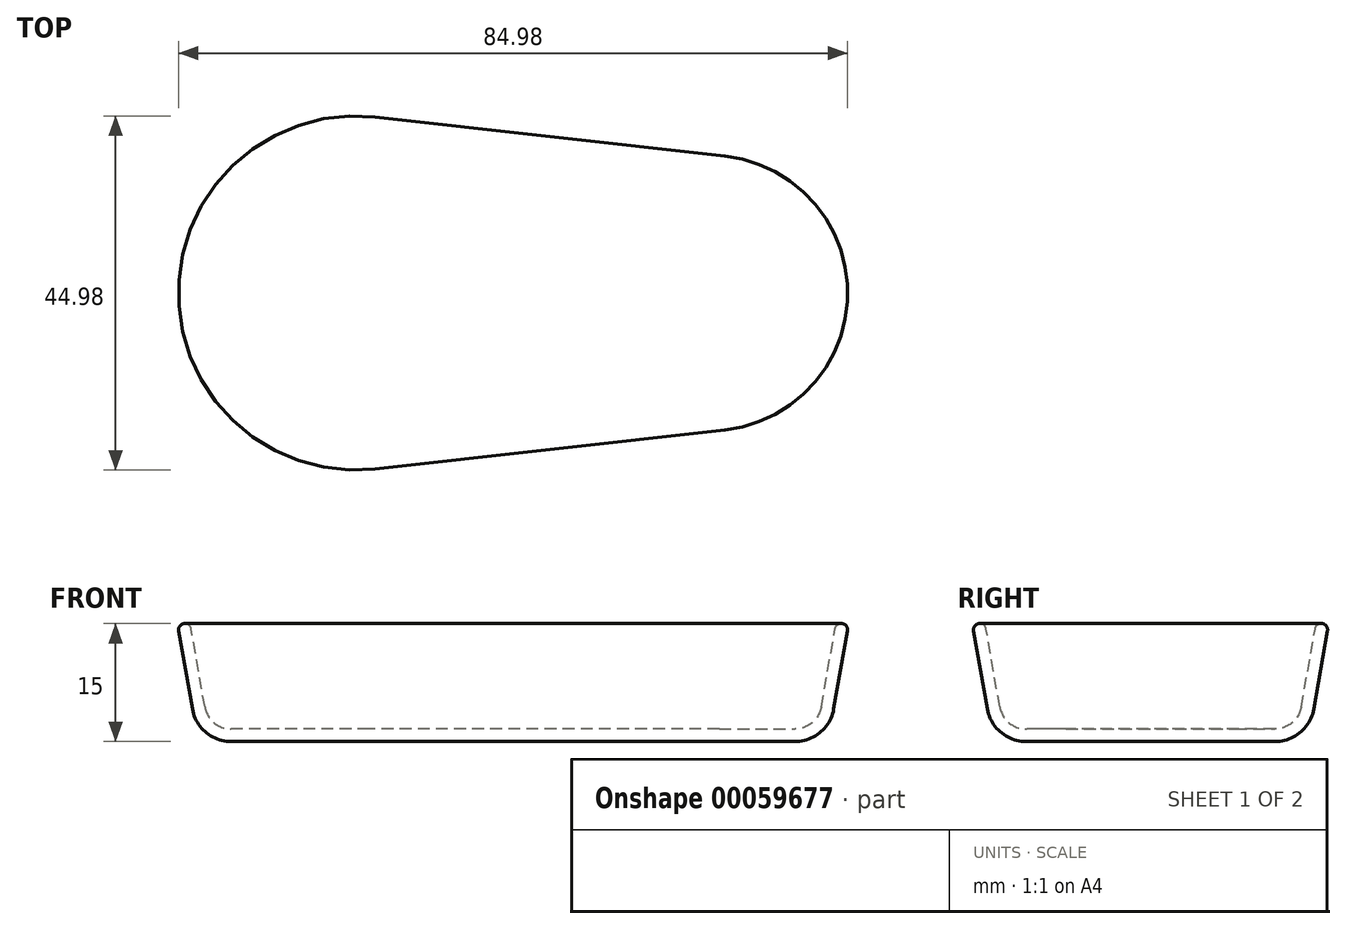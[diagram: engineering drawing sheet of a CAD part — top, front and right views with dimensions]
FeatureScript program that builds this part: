
annotation { "Feature Type Name" : "Feature", "Feature Type Description" : "" }
export const myFeature = defineFeature(function(context is Context, id is Id, definition is map)
    precondition{}
    {
        {
            var Q0;
            Q0=qCreatedBy(makeId("Top.planeOp"),FACE);
            var sketch = newSketch(context, id + "F0", { "sketchPlane" : qUnion([Q0])});
            skLineSegment(sketch, "E0.bottom", {"start": v(-20, 20) * mm, "end": v(60, 20) * mm});
            skLineSegment(sketch, "E0.top", {"start": v(-20, -20) * mm, "end": v(60, -20) * mm});
            skLineSegment(sketch, "E0.left", {"start": v(-20, 20) * mm, "end": v(-20, -20) * mm});
            skLineSegment(sketch, "E0.right", {"start": v(60, 20) * mm, "end": v(60, -20) * mm});
            skArc(sketch, "E1", {"start": v(2.22, 19.88) * mm, "mid": v(-20, 0) * mm, "end": v(2.22, -19.88) * mm});
            skArc(sketch, "E2", {"start": v(46.67, -14.9) * mm, "mid": v(60, 0) * mm, "end": v(46.67, 14.9) * mm});
            skLineSegment(sketch, "E3", {"start": v(2.22, 19.88) * mm, "end": v(46.67, 14.9) * mm});
            skLineSegment(sketch, "E4", {"start": v(2.22, -19.88) * mm, "end": v(46.67, -14.9) * mm});
            skSolve(sketch);
        }
        {
            var Q0;
            {var subQ5=sQuery(id+"F0.wireOp",EDGE,"E3");Q0=makeQuery(id+"F0.imprint","IMPRINT",FACE,{"disambiguationData":[TD([[makeQuery(id+"F0.imprint","IMPRINT",EDGE,{"derivedFrom":subQ5}),-1.0]])]});}
            extrude(context, id + "F1", {"entities" : qUnion([Q0]), "depth" : 15 * mm, "hasDraft" : true, "draftAngle" : 10 * degree});
        }
        {
            var Q0;
            Q0=makeQuery(id+"F1.opExtrude","CAP_EDGE",EDGE,{"disambiguationData":[OSD([sQuery(id+"F0.wireOp",EDGE,"E1")])],"isStart":true});
            fillet(context, id + "F2", {"entities" : qUnion([Q0]), "radius" : 5 * mm, "tangentPropagation" : true, "allowEdgeOverflow" : false});
        }
        {
            var Q0;
            Q0=makeQuery(id+"F1.opExtrude","CAP_FACE",FACE,{"disambiguationData":[OSD([sQuery(id+"F0.wireOp",EDGE,"E0.bottom"),sQuery(id+"F0.wireOp",EDGE,"E0.top"),sQuery(id+"F0.wireOp",EDGE,"E0.left"),sQuery(id+"F0.wireOp",EDGE,"E0.right")])],"isStart":false});
            var Q1;
            Q1=makeQuery(id+"F1.opExtrude","CAP_FACE",FACE,{"disambiguationData":[OSD([sQuery(id+"F0.wireOp",EDGE,"E1"),sQuery(id+"F0.wireOp",EDGE,"E2"),sQuery(id+"F0.wireOp",EDGE,"E3"),sQuery(id+"F0.wireOp",EDGE,"E4")])],"isStart":false});
            shell(context, id + "F3", {"entities" : qUnion([Q0, Q1]), "thickness" : 1.6 * mm});
        }
        {
            var Q0;
            Q0=makeQuery(id+"F1.opExtrude","CAP_EDGE",EDGE,{"disambiguationData":[OSD([sQuery(id+"F0.wireOp",EDGE,"E1")])],"isStart":false});
            var Q1;
            {var subQ0=sQuery(id+"F0.wireOp",EDGE,"E1");Q1=makeQuery(id+"F3.opShell","OFFSET_EDGE",EDGE,{"disambiguationData":[OSD([subQ0]),TDD([makeQuery(id+"F1.opExtrude","CAP_EDGE",EDGE,{"disambiguationData":[OSD([subQ0])],"isStart":false})])]});}
            fillet(context, id + "F4", {"entities" : qUnion([Q0, Q1]), "radius" : .8 * mm, "tangentPropagation" : true, "allowEdgeOverflow" : false});
        }
    });
